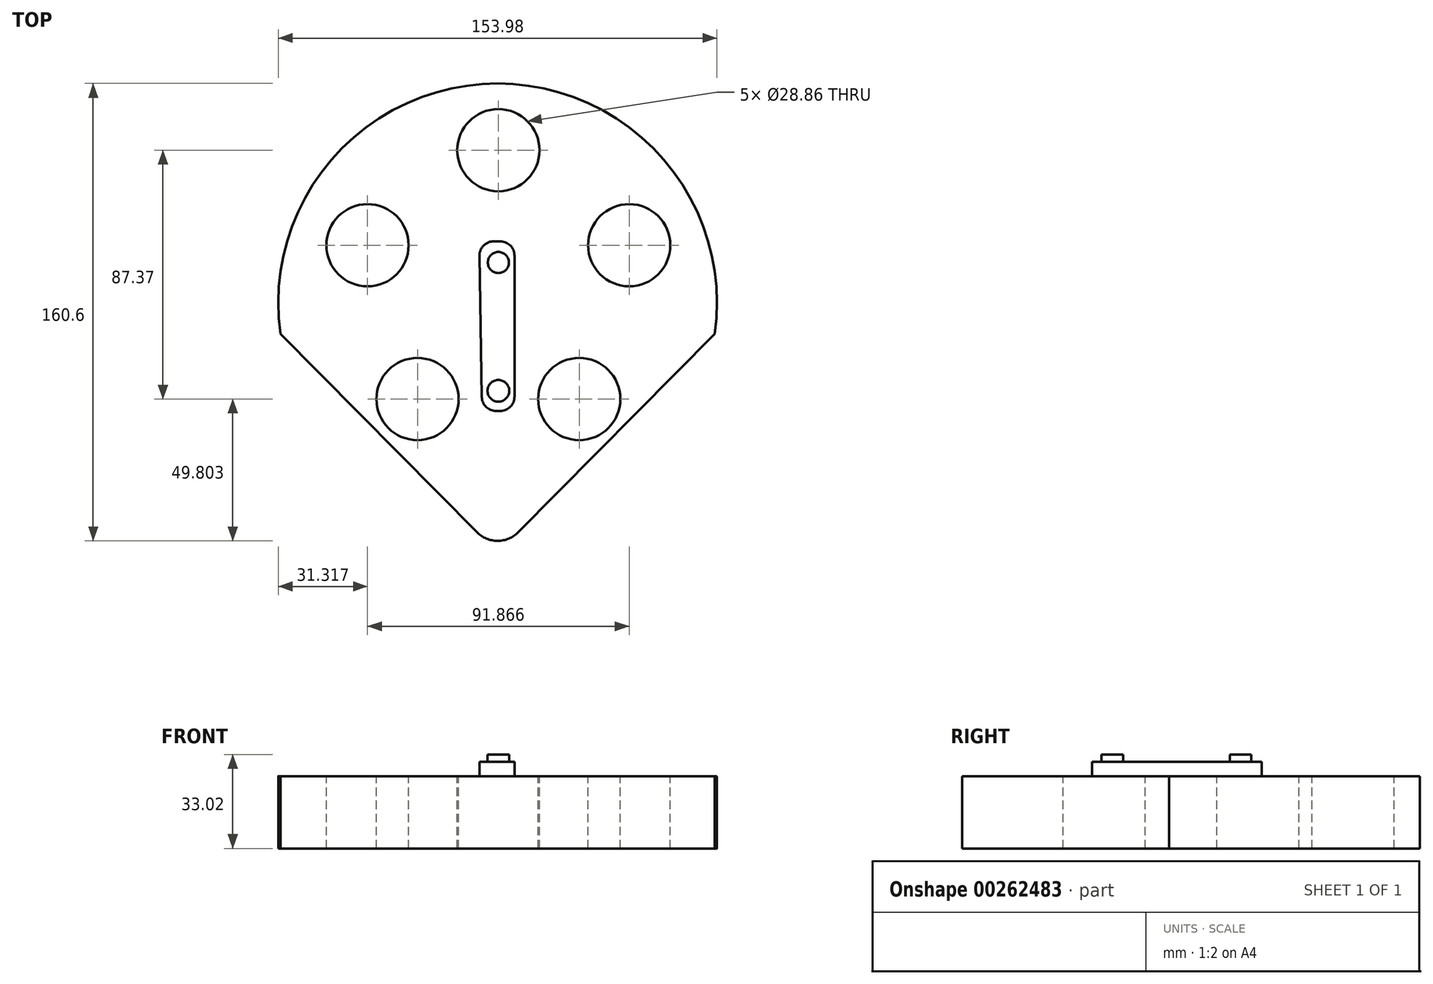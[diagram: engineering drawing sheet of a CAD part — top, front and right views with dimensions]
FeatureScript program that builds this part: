
annotation { "Feature Type Name" : "Feature", "Feature Type Description" : "" }
export const myFeature = defineFeature(function(context is Context, id is Id, definition is map)
    precondition{}
    {
        {
            var Q0;
            Q0=qCreatedBy(makeId("Top.planeOp"),FACE);
            var sketch = newSketch(context, id + "F0", { "sketchPlane" : qUnion([Q0])});
            skArc(sketch, "E0", {"start": v(75.94, 0) * mm, "mid": v(-0.26, 87.98) * mm, "end": v(-76.46, 0) * mm});
            skLineSegment(sketch, "E1", {"start": v(-76.46, 0) * mm, "end": v(-0.26, -76.9) * mm});
            skLineSegment(sketch, "E2", {"start": v(75.94, 0) * mm, "end": v(-0.26, -76.9) * mm});
            skSolve(sketch);
        }
        {
            var Q0;
            Q0=makeQuery(id+"F0.imprint","IMPRINT",FACE,{"disambiguationData":[TD([[makeQuery(id+"F0.imprint","IMPRINT",EDGE,{"derivedFrom":sQuery(id+"F0.wireOp",EDGE,"E0")}),1.0]])]});
            extrude(context, id + "F1", {"entities" : qUnion([Q0]), "depth" : 25.4 * mm});
        }
        {
            var Q0;
            Q0=makeQuery(id+"F1.opExtrude","SWEPT_EDGE",EDGE,{"disambiguationData":[OSD([sQuery(id+"F0.wireOp",EDGE,"E1"),sQuery(id+"F0.wireOp",EDGE,"E2")])]});
            fillet(context, id + "F2", {"entities" : qUnion([Q0]), "radius" : 10.16 * mm, "tangentPropagation" : true, "allowEdgeOverflow" : false});
        }
        {
            var Q0;
            Q0=makeQuery(id+"F1.opExtrude","CAP_FACE",FACE,{"disambiguationData":[OSD([sQuery(id+"F0.wireOp",EDGE,"E0"),sQuery(id+"F0.wireOp",EDGE,"E1"),sQuery(id+"F0.wireOp",EDGE,"E2")])],"isStart":false});
            var sketch = newSketch(context, id + "F3", { "sketchPlane" : qUnion([Q0])});
            skCircle(sketch, "E3", {"center": v(0, 64.55) * mm, "radius": 14.43 * mm});
            skCircle(sketch, "E4.1.0", {"center": v(-45.93, 31.18) * mm, "radius": 14.43 * mm});
            skCircle(sketch, "E4.2.0", {"center": v(-28.39, -22.82) * mm, "radius": 14.43 * mm});
            skCircle(sketch, "E4.3.0", {"center": v(28.39, -22.82) * mm, "radius": 14.43 * mm});
            skCircle(sketch, "E4.4.0", {"center": v(45.93, 31.18) * mm, "radius": 14.43 * mm});
            skPoint(sketch, "E4.center", {"position": v(0, 16.26) * mm});
            skSolve(sketch);
        }
        {
            var Q0;
            Q0 = qSketchRegion(id + "F3", true);
            extrude(context, id + "F4", {"entities" : qUnion([Q0]), "operationType" : NewBodyOperationType.REMOVE, "endBound" : BoundingType.THROUGH_ALL, "oppositeDirection" : true, "depth" : 25.4 * mm});
        }
        {
            var Q0;
            Q0=makeQuery(id+"F1.opExtrude","CAP_FACE",FACE,{"disambiguationData":[OSD([sQuery(id+"F0.wireOp",EDGE,"E0"),sQuery(id+"F0.wireOp",EDGE,"E1"),sQuery(id+"F0.wireOp",EDGE,"E2")])],"isStart":false});
            var sketch = newSketch(context, id + "F5", { "sketchPlane" : qUnion([Q0])});
            skLineSegment(sketch, "E5", {"start": v(-6.73, 32.58) * mm, "end": v(5.66, 32.58) * mm});
            skPoint(sketch, "E6.end.orphan", {"position": v(0, -2.92) * mm});
            skLineSegment(sketch, "E7", {"start": v(5.66, 32.58) * mm, "end": v(5.66, -27.03) * mm});
            skLineSegment(sketch, "E8", {"start": v(5.66, -27.03) * mm, "end": v(-5.72, -27.03) * mm});
            skLineSegment(sketch, "E9", {"start": v(-5.72, -27.03) * mm, "end": v(-6.73, 32.58) * mm});
            skSolve(sketch);
        }
        {
            var Q0;
            Q0 = qSketchRegion(id + "F5", true);
            extrude(context, id + "F6", {"entities" : qUnion([Q0]), "operationType" : NewBodyOperationType.ADD, "depth" : 5.08 * mm});
        }
        {
            var Q0;
            Q0=makeQuery(id+"F6.opExtrude","CAP_FACE",FACE,{"disambiguationData":[OSD([sQuery(id+"F5.wireOp",EDGE,"E5"),sQuery(id+"F5.wireOp",EDGE,"E7"),sQuery(id+"F5.wireOp",EDGE,"E8"),sQuery(id+"F5.wireOp",EDGE,"E9")])],"isStart":false});
            var sketch = newSketch(context, id + "F7", { "sketchPlane" : qUnion([Q0])});
            skCircle(sketch, "E10", {"center": v(0, 25.12) * mm, "radius": 3.7 * mm});
            skCircle(sketch, "E11", {"center": v(0, -19.95) * mm, "radius": 3.81 * mm});
            skSolve(sketch);
        }
        {
            var Q0;
            Q0 = qSketchRegion(id + "F7", true);
            extrude(context, id + "F8", {"entities" : qUnion([Q0]), "operationType" : NewBodyOperationType.ADD, "depth" : 2.54 * mm});
        }
        {
            var Q0;
            Q0=makeQuery(id+"F6.opExtrude","SWEPT_EDGE",EDGE,{"disambiguationData":[OSD([sQuery(id+"F5.wireOp",EDGE,"E8"),sQuery(id+"F5.wireOp",EDGE,"E9")])]});
            var Q1;
            Q1=makeQuery(id+"F6.opExtrude","SWEPT_EDGE",EDGE,{"disambiguationData":[OSD([sQuery(id+"F5.wireOp",EDGE,"E7"),sQuery(id+"F5.wireOp",EDGE,"E8")])]});
            var Q2;
            Q2=makeQuery(id+"F6.opExtrude","SWEPT_EDGE",EDGE,{"disambiguationData":[OSD([sQuery(id+"F5.wireOp",EDGE,"E5"),sQuery(id+"F5.wireOp",EDGE,"E7")])]});
            var Q3;
            Q3=makeQuery(id+"F6.opExtrude","SWEPT_EDGE",EDGE,{"disambiguationData":[OSD([sQuery(id+"F5.wireOp",EDGE,"E5"),sQuery(id+"F5.wireOp",EDGE,"E9")])]});
            fillet(context, id + "F9", {"entities" : qUnion([Q0, Q1, Q2, Q3]), "radius" : 5.08 * mm, "tangentPropagation" : true, "allowEdgeOverflow" : false});
        }
    });
